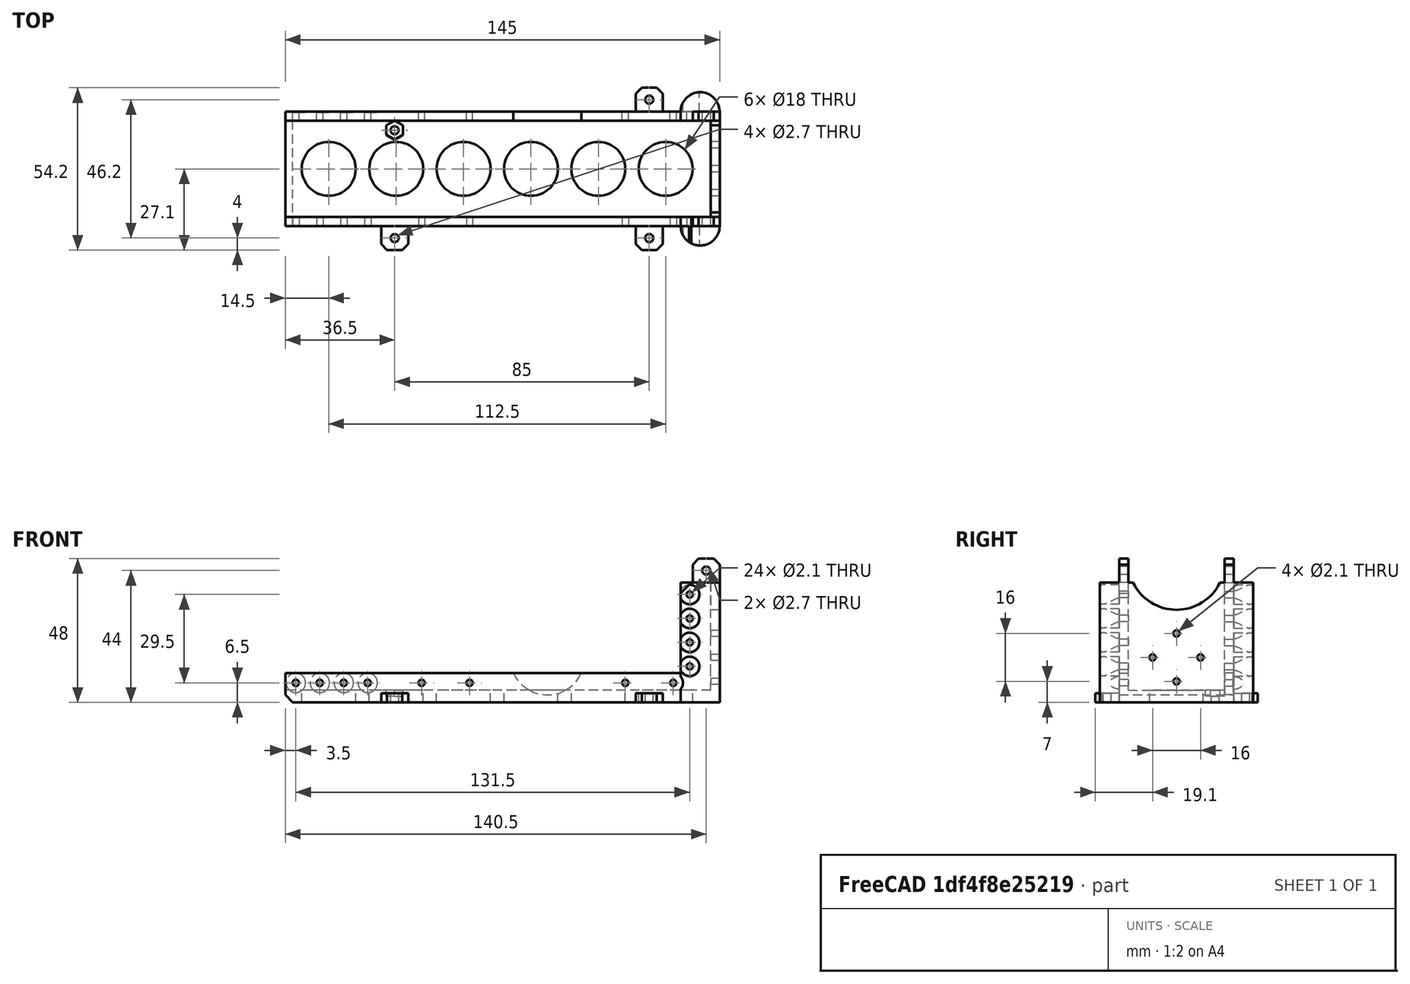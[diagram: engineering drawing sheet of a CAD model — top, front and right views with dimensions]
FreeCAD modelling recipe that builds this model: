
FCSTD DOCUMENT  (FreeCAD 0.15R4671 (Git))
Label: elbow_roll_frame_4_servo
License: CC-BY 3.0
LicenseURL: http://creativecommons.org/licenses/by/3.0/
objects: Part::Cylinder×60, Part::MultiFuse×35, Part::Box×12, Part::Cut×8, Part::Chamfer×4, Part::Mirroring×3, Part::Extrusion×1
note: 123 computed .brp shape members not serialized (recipe doc carries the construction recipe); baked Part::Feature solids carry a one-line shape summary decoded from their .brp

FEATURE [Part::Box] Box  label="Cube"
  Height = 3
  Length = 36
  Width = 38.2
FEATURE [Part::Box] Box001  label="Cube001"
  Height = 10
  Length = 36
  Placement = pos=(0,0,3) rot=(0,0,1;0rad)
  Width = 3
FEATURE [Part::Box] Box002  label="Cube002"
  Height = 10
  Length = 36
  Placement = pos=(0,35.2,3) rot=(0,0,1;0rad)
  Width = 3
FEATURE [Part::Cylinder] Cylinder
  Angle = 360
  Height = 40
  Placement = pos=(-4,0,6.5) rot=(0,1,0;1.5708rad)
  Radius = 6.5
FEATURE [Part::Box] Box003  label="Cube003"
  Height = 20
  Length = 50
  Placement = pos=(-10,0,-5) rot=(0,0,1;0rad)
  Width = 10
FEATURE [Part::Cut] Cut
  Base = -> Cylinder
  Tool = -> Box003
FEATURE [Part::Box] Box004  label="Cube004"
  Height = 20
  Length = 50
  Placement = pos=(-10,0,-5) rot=(0,0,1;0rad)
  Width = 10
FEATURE [Part::Cylinder] Cylinder001
  Angle = 360
  Height = 40
  Placement = pos=(0,0,6.5) rot=(0,1,0;1.5708rad)
  Radius = 6.5
FEATURE [Part::Cut] Cut001
  Base = -> Cylinder001
  Placement = pos=(36,38.2,0) rot=(0,0,1;3.14159rad)
  Tool = -> Box004
FEATURE [Part::MultiFuse] Fusion
  Shapes = -> [Box,Box002,Box001,Cut,Cut001]
FEATURE [Part::Cylinder] Cylinder003
  Angle = 360
  Height = 15
  Placement = pos=(16,4,10) rot=(1,0,0;1.5708rad)
  Radius = 1.05
FEATURE [Part::Cylinder] Cylinder004
  Angle = 360
  Height = 15
  Placement = pos=(24,4,10) rot=(1,0,0;1.5708rad)
  Radius = 1.05
FEATURE [Part::Cylinder] Cylinder005
  Angle = 360
  Height = 15
  Placement = pos=(32,4,10) rot=(1,0,0;1.5708rad)
  Radius = 1.05
FEATURE [Part::Cylinder] Cylinder006
  Angle = 360
  Height = 10
  Placement = pos=(8,0,10) rot=(1,0,0;1.5708rad)
  Radius = 3.25
FEATURE [Part::Cylinder] Cylinder007
  Angle = 360
  Height = 10
  Placement = pos=(8,0,10) rot=(1,0,0;1.5708rad)
  Radius = 3.25
FEATURE [Part::Cylinder] Cylinder008
  Angle = 360
  Height = 10
  Placement = pos=(16,0,10) rot=(1,0,0;1.5708rad)
  Radius = 3.25
FEATURE [Part::Cylinder] Cylinder009
  Angle = 360
  Height = 15
  Placement = pos=(8,4,10) rot=(1,0,0;1.5708rad)
  Radius = 1.05
FEATURE [Part::Cylinder] Cylinder010
  Angle = 360
  Height = 10
  Placement = pos=(24,0,10) rot=(1,0,0;1.5708rad)
  Radius = 3.25
FEATURE [Part::Cylinder] Cylinder011
  Angle = 360
  Height = 10
  Placement = pos=(32,0,10) rot=(1,0,0;1.5708rad)
  Radius = 3.25
FEATURE [Part::MultiFuse] Fusion001
  Shapes = -> [Cylinder003,Cylinder008,Cylinder007,Cylinder005,Cylinder011,Cylinder006,Cylinder010,Cylinder009,Cylinder004]
FEATURE [Part::Cylinder] Cylinder012
  Angle = 360
  Height = 15
  Placement = pos=(24,4,10) rot=(1,0,0;1.5708rad)
  Radius = 1.05
FEATURE [Part::Cylinder] Cylinder013
  Angle = 360
  Height = 15
  Placement = pos=(8,4,10) rot=(1,0,0;1.5708rad)
  Radius = 1.05
FEATURE [Part::Cylinder] Cylinder014
  Angle = 360
  Height = 10
  Placement = pos=(24,0,10) rot=(1,0,0;1.5708rad)
  Radius = 3.25
FEATURE [Part::Cylinder] Cylinder015
  Angle = 360
  Height = 10
  Placement = pos=(8,0,10) rot=(1,0,0;1.5708rad)
  Radius = 3.25
FEATURE [Part::Cylinder] Cylinder016
  Angle = 360
  Height = 10
  Placement = pos=(32,0,10) rot=(1,0,0;1.5708rad)
  Radius = 3.25
FEATURE [Part::Cylinder] Cylinder017
  Angle = 360
  Height = 10
  Placement = pos=(8,0,10) rot=(1,0,0;1.5708rad)
  Radius = 3.25
FEATURE [Part::Cylinder] Cylinder018
  Angle = 360
  Height = 15
  Placement = pos=(32,4,10) rot=(1,0,0;1.5708rad)
  Radius = 1.05
FEATURE [Part::Cylinder] Cylinder019
  Angle = 360
  Height = 10
  Placement = pos=(16,0,10) rot=(1,0,0;1.5708rad)
  Radius = 3.25
FEATURE [Part::Cylinder] Cylinder020
  Angle = 360
  Height = 15
  Placement = pos=(16,4,10) rot=(1,0,0;1.5708rad)
  Radius = 1.05
FEATURE [Part::MultiFuse] Fusion002
  Placement = pos=(40,38.2,0) rot=(0,0,1;3.14159rad)
  Shapes = -> [Cylinder020,Cylinder019,Cylinder017,Cylinder018,Cylinder016,Cylinder015,Cylinder014,Cylinder013,Cylinder012]
FEATURE [Part::MultiFuse] Fusion003
  Shapes = -> [Fusion001,Fusion002]
FEATURE [Part::Cylinder] Cylinder022
  Angle = 360
  Height = 10
  Placement = pos=(3,19.1,-3) rot=(0,0,1;0rad)
  Radius = 1.05
FEATURE [Part::Cylinder] Cylinder023
  Angle = 360
  Height = 10
  Placement = pos=(19,19.1,-3) rot=(0,0,1;0rad)
  Radius = 1.05
FEATURE [Part::Cylinder] Cylinder024
  Angle = 360
  Height = 10
  Placement = pos=(11,11.1,-3) rot=(0,0,1;0rad)
  Radius = 1.05
FEATURE [Part::Cylinder] Cylinder025
  Angle = 360
  Height = 10
  Placement = pos=(11,27.1,-3) rot=(0,0,1;0rad)
  Radius = 1.05
FEATURE [Part::MultiFuse] Fusion004
  Shapes = -> [Cylinder022,Cylinder025,Cylinder023,Cylinder024]
FEATURE [Part::Cylinder] Cylinder026
  Angle = 360
  Height = 10
  Placement = pos=(43,19.1,-3) rot=(0,0,1;0rad)
  Radius = 16.1
FEATURE [Part::MultiFuse] Fusion006
  Shapes = -> [Fusion004,Fusion003]
FEATURE [Part::Box] Box005  label="Cube005"
  Height = 10
  Length = 10
  Placement = pos=(29.5,-10,16) rot=(0,1,0;0.785398rad)
  Width = 20
FEATURE [Part::Box] Box006  label="Cube006"
  Height = 145
  Length = 4
  Placement = pos=(-4,0,0) rot=(0,0,1;0rad)
  Width = 38.2
FEATURE [Part::Box] Box007  label="Cube007"
  Height = 145
  Length = 5.75
  Width = 3
FEATURE [Part::Box] Box008  label="Cube008"
  Height = 145
  Length = 5.75
  Placement = pos=(0,35.2,0) rot=(0,0,1;0rad)
  Width = 3
FEATURE [Part::Cylinder] Cylinder027
  Angle = 360
  Height = 3
  Placement = pos=(11,38.2,57.5) rot=(1,0,0;1.5708rad)
  Radius = 12.5
FEATURE [Part::MultiFuse] Fusion007
  Shapes = -> [Cylinder027,Box005,Cylinder026]
FEATURE [Part::MultiFuse] Fusion008
  Shapes = -> [Fusion,Box006,Box007,Box008]
FEATURE [Part::Cylinder] Cylinder028
  Angle = 360
  Height = 15
  Placement = pos=(2.5,4,15.5) rot=(1,0,0;1.5708rad)
  Radius = 1.05
FEATURE [Part::Cylinder] Cylinder029
  Angle = 360
  Height = 10
  Placement = pos=(2.5,0,15.5) rot=(1,0,0;1.5708rad)
  Radius = 3.25
FEATURE [Part::MultiFuse] Fusion009
  Shapes = -> [Cylinder028,Cylinder029]
FEATURE [Part::Cylinder] Cylinder030
  Angle = 360
  Height = 10
  Placement = pos=(2.5,0,15.5) rot=(1,0,0;1.5708rad)
  Radius = 3.25
FEATURE [Part::Cylinder] Cylinder031
  Angle = 360
  Height = 15
  Placement = pos=(2.5,4,15.5) rot=(1,0,0;1.5708rad)
  Radius = 1.05
FEATURE [Part::MultiFuse] Fusion010
  Placement = pos=(0,0,16) rot=(0,0,1;0rad)
  Shapes = -> [Cylinder031,Cylinder030]
FEATURE [Part::Cylinder] Cylinder036
  Angle = 360
  Height = 10
  Placement = pos=(2.5,0,15.5) rot=(1,0,0;1.5708rad)
  Radius = 3.25
FEATURE [Part::Cylinder] Cylinder037
  Angle = 360
  Height = 15
  Placement = pos=(2.5,4,15.5) rot=(1,0,0;1.5708rad)
  Radius = 1.05
FEATURE [Part::MultiFuse] Fusion013
  Placement = pos=(0,0,68) rot=(0,0,1;0rad)
  Shapes = -> [Cylinder037,Cylinder036]
FEATURE [Part::Cylinder] Cylinder038
  Angle = 360
  Height = 10
  Placement = pos=(2.5,0,15.5) rot=(1,0,0;1.5708rad)
  Radius = 3.25
FEATURE [Part::Cylinder] Cylinder039
  Angle = 360
  Height = 15
  Placement = pos=(2.5,4,15.5) rot=(1,0,0;1.5708rad)
  Radius = 1.05
FEATURE [Part::MultiFuse] Fusion014
  Placement = pos=(0,0,84) rot=(0,0,1;0rad)
  Shapes = -> [Cylinder039,Cylinder038]
FEATURE [Part::MultiFuse] Fusion015
  Shapes = -> [Fusion014,Fusion013,Fusion010,Fusion009]
FEATURE [Part::MultiFuse] Fusion017
  Shapes = -> [Cylinder028,Cylinder029]
FEATURE [Part::MultiFuse] Fusion018
  Placement = pos=(0,0,16) rot=(0,0,1;0rad)
  Shapes = -> [Cylinder031,Cylinder030]
FEATURE [Part::MultiFuse] Fusion019
  Placement = pos=(0,0,68) rot=(0,0,1;0rad)
  Shapes = -> [Cylinder037,Cylinder036]
FEATURE [Part::MultiFuse] Fusion020
  Placement = pos=(0,0,84) rot=(0,0,1;0rad)
  Shapes = -> [Cylinder039,Cylinder038]
FEATURE [Part::MultiFuse] Fusion016
  Placement = pos=(5,38.2,0) rot=(0,0,1;3.14159rad)
  Shapes = -> [Fusion020,Fusion019,Fusion018,Fusion017]
FEATURE [Part::Cut] Cut002
  Base = -> Fusion008
  Tool = -> Fusion007
FEATURE [Part::Cylinder] Cylinder040 .. Cylinder043  x4 (patterned run collapsed; names and placements below)
  Angle = 360
  Height = 10
  Radius = 9
  placements: 4 in arithmetic series — first pos=(-5,19.1,20) rot=(0,1,0;1.5708rad), step (0,0,22.5), last pos=(-5,19.1,87.5) rot=(0,1,0;1.5708rad)
FEATURE [Part::Cylinder] Cylinder046
  Angle = 360
  Height = 10
  Placement = pos=(2.5,0,15.5) rot=(1,0,0;1.5708rad)
  Radius = 3.25
FEATURE [Part::Cylinder] Cylinder047
  Angle = 360
  Height = 15
  Placement = pos=(2.5,4,15.5) rot=(1,0,0;1.5708rad)
  Radius = 1.05
FEATURE [Part::MultiFuse] Fusion024
  Placement = pos=(0,0,102) rot=(0,0,1;0rad)
  Shapes = -> [Cylinder047,Cylinder046]
FEATURE [Part::Cylinder] Cylinder048
  Angle = 360
  Height = 10
  Placement = pos=(2.5,0,15.5) rot=(1,0,0;1.5708rad)
  Radius = 3.25
FEATURE [Part::Cylinder] Cylinder049
  Angle = 360
  Height = 15
  Placement = pos=(2.5,4,15.5) rot=(1,0,0;1.5708rad)
  Radius = 1.05
FEATURE [Part::MultiFuse] Fusion025
  Placement = pos=(0,0,110) rot=(0,0,1;0rad)
  Shapes = -> [Cylinder049,Cylinder048]
FEATURE [Part::Cylinder] Cylinder050
  Angle = 360
  Height = 10
  Placement = pos=(2.5,0,15.5) rot=(1,0,0;1.5708rad)
  Radius = 3.25
FEATURE [Part::Cylinder] Cylinder051
  Angle = 360
  Height = 15
  Placement = pos=(2.5,4,15.5) rot=(1,0,0;1.5708rad)
  Radius = 1.05
FEATURE [Part::MultiFuse] Fusion026
  Placement = pos=(0,0,118) rot=(0,0,1;0rad)
  Shapes = -> [Cylinder051,Cylinder050]
FEATURE [Part::Cylinder] Cylinder052
  Angle = 360
  Height = 10
  Placement = pos=(2.5,0,15.5) rot=(1,0,0;1.5708rad)
  Radius = 3.25
FEATURE [Part::Cylinder] Cylinder053
  Angle = 360
  Height = 15
  Placement = pos=(2.5,4,15.5) rot=(1,0,0;1.5708rad)
  Radius = 1.05
FEATURE [Part::MultiFuse] Fusion027
  Placement = pos=(0,0,126) rot=(0,0,1;0rad)
  Shapes = -> [Cylinder053,Cylinder052]
FEATURE [Part::MultiFuse] Fusion028
  Shapes = -> [Fusion027,Fusion026,Fusion025,Fusion024]
FEATURE [Part::Cylinder] Cylinder054
  Angle = 360
  Height = 10
  Placement = pos=(2.5,0,15.5) rot=(1,0,0;1.5708rad)
  Radius = 3.25
FEATURE [Part::Cylinder] Cylinder055
  Angle = 360
  Height = 15
  Placement = pos=(2.5,4,15.5) rot=(1,0,0;1.5708rad)
  Radius = 1.05
FEATURE [Part::MultiFuse] Fusion029
  Placement = pos=(0,0,102) rot=(0,0,1;0rad)
  Shapes = -> [Cylinder055,Cylinder054]
FEATURE [Part::Cylinder] Cylinder056
  Angle = 360
  Height = 10
  Placement = pos=(2.5,0,15.5) rot=(1,0,0;1.5708rad)
  Radius = 3.25
FEATURE [Part::Cylinder] Cylinder057
  Angle = 360
  Height = 15
  Placement = pos=(2.5,4,15.5) rot=(1,0,0;1.5708rad)
  Radius = 1.05
FEATURE [Part::MultiFuse] Fusion030
  Placement = pos=(0,0,110) rot=(0,0,1;0rad)
  Shapes = -> [Cylinder057,Cylinder056]
FEATURE [Part::Cylinder] Cylinder058
  Angle = 360
  Height = 10
  Placement = pos=(2.5,0,15.5) rot=(1,0,0;1.5708rad)
  Radius = 3.25
FEATURE [Part::Cylinder] Cylinder059
  Angle = 360
  Height = 15
  Placement = pos=(2.5,4,15.5) rot=(1,0,0;1.5708rad)
  Radius = 1.05
FEATURE [Part::MultiFuse] Fusion031
  Placement = pos=(0,0,118) rot=(0,0,1;0rad)
  Shapes = -> [Cylinder059,Cylinder058]
FEATURE [Part::Cylinder] Cylinder060
  Angle = 360
  Height = 10
  Placement = pos=(2.5,0,15.5) rot=(1,0,0;1.5708rad)
  Radius = 3.25
FEATURE [Part::Cylinder] Cylinder061
  Angle = 360
  Height = 15
  Placement = pos=(2.5,4,15.5) rot=(1,0,0;1.5708rad)
  Radius = 1.05
FEATURE [Part::MultiFuse] Fusion032
  Placement = pos=(0,0,126) rot=(0,0,1;0rad)
  Shapes = -> [Cylinder061,Cylinder060]
FEATURE [Part::MultiFuse] Fusion033
  Placement = pos=(5,38,0) rot=(0,0,1;3.14159rad)
  Shapes = -> [Fusion032,Fusion031,Fusion030,Fusion029]
FEATURE [Part::Cylinder] Cylinder062
  Angle = 360
  Height = 10
  Placement = pos=(-5,19.1,110) rot=(0,1,0;1.5708rad)
  Radius = 9
FEATURE [Part::Cylinder] Cylinder063
  Angle = 360
  Height = 10
  Placement = pos=(-5,19.1,132.5) rot=(0,1,0;1.5708rad)
  Radius = 9
FEATURE [Part::MultiFuse] Fusion034
  Placement = pos=(0,0,-2) rot=(0,0,1;0rad)
  Shapes = -> [Cylinder062,Cylinder043,Cylinder042,Cylinder040,Cylinder063,Cylinder041]
FEATURE [Part::MultiFuse] Fusion035
  Shapes = -> [Fusion034,Fusion033,Fusion028,Fusion006,Fusion015,Fusion016]
FEATURE [Part::Chamfer] Chamfer
  Base = -> Cut002
  Edges = 1 edges r=2.5: [Edge5]
FEATURE [Part::Cut] Cut003
  Base = -> Chamfer
  Placement = pos=(0,0,0) rot=(0,-1,0;1.5708rad)
  Tool = -> Fusion035
FEATURE [Part::Box] Box009  label="Cube009"
  Height = 8
  Length = 9
  Placement = pos=(-9,0,36) rot=(0,0,1;0rad)
  Width = 3
FEATURE [Part::Cylinder] Cylinder064
  Angle = 360
  Height = 10
  Placement = pos=(-4.5,5,40) rot=(1,0,0;1.5708rad)
  Radius = 1.35
FEATURE [Part::Cut] Cut004
  Base = -> Box009
  Tool = -> Cylinder064
FEATURE [Part::Chamfer] Chamfer001
  Base = -> Cut004
  Edges = 2 edges r=2: [Edge2,Edge10]
FEATURE [Part::Box] Box010  label="Cube010"
  Height = 8
  Length = 9
  Placement = pos=(-9,0,36) rot=(0,0,1;0rad)
  Width = 3
FEATURE [Part::Cylinder] Cylinder065
  Angle = 360
  Height = 10
  Placement = pos=(-4.5,5,40) rot=(1,0,0;1.5708rad)
  Radius = 1.35
FEATURE [Part::Cut] Cut005
  Base = -> Box010
  Tool = -> Cylinder065
FEATURE [Part::Chamfer] Chamfer002
  Base = -> Cut005
  Edges = 2 edges r=2: [Edge2,Edge10]
  Placement = pos=(0,35.2,0) rot=(0,0,1;0rad)
FEATURE [Part::MultiFuse] Fusion036
  Shapes = -> [Chamfer001,Chamfer002]
FEATURE [Part::Box] Box011  label="Cube011"
  Height = 8
  Length = 9
  Placement = pos=(-9,0,36) rot=(0,0,1;0rad)
  Width = 3
FEATURE [Part::Cylinder] Cylinder066
  Angle = 360
  Height = 10
  Placement = pos=(-4.5,5,40) rot=(1,0,0;1.5708rad)
  Radius = 1.35
FEATURE [Part::Cut] Cut006
  Base = -> Box011
  Tool = -> Cylinder066
FEATURE [Part::Chamfer] Chamfer003
  Base = -> Cut006
  Edges = 2 edges r=2: [Edge2,Edge10]
  Placement = pos=(-19,2.2,-1) rot=(-1,0,0;1.5708rad)
FEATURE [Part::Mirroring] Part__Mirroring  label="Chamfer003 (Mirror #1)"
  Base = (0,19.1,0)
  Normal = (0,1,0)
  Source = -> Chamfer003
FEATURE [Part::Mirroring] Part__Mirroring001  label="Chamfer003 (Mirror #2)"
  Base = (-66,0,0)
  Normal = (1,0,0)
  Source = -> Part__Mirroring
FEATURE [Part::Cylinder] Cylinder067
  Angle = 360
  Height = 10
  Placement = pos=(-108.5,32,-6) rot=(0,0,1;0rad)
  Radius = 1.35
FEATURE [Part::Extrusion] Extrude
  Dir = (0,0,2)
  Placement = pos=(0,11,0) rot=(0,0,1;0rad)
  Solid = true
FEATURE [Part::Mirroring] Part__Mirroring002  label="Extrude (Mirror #1)001"
  Base = (0,0,0)
  Normal = (1,0,0)
  Source = -> Extrude
FEATURE [Part::MultiFuse] Fusion037
  Placement = pos=(-108.5,21,-2) rot=(0,0,1;0rad)
  Shapes = -> [Part__Mirroring002,Extrude]
FEATURE [Part::MultiFuse] Fusion038
  Shapes = -> [Fusion037,Cylinder067]
FEATURE [Part::MultiFuse] Fusion039
  Shapes = -> [Chamfer003,Part__Mirroring,Part__Mirroring001,Fusion036]
FEATURE [Part::MultiFuse] Fusion040
  Shapes = -> [Cut003,Fusion039]
FEATURE [Part::Cut] Cut007
  Base = -> Fusion040
  Tool = -> Fusion038
